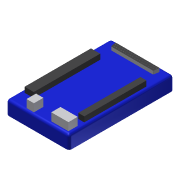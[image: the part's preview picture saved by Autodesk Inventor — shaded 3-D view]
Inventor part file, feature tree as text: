
AUTODESK INVENTOR PART (.ipt)
format: ipt  version: 2013 (Build 170138000, 138)  size: 187,904 bytes
history: native  units: in
note: dims shown in document units (in); Inventor stores cm internally (conversion verified against a paired STEP export)
features: extrude x4, sketch x4, other x3, fillet x1
ambient origin geometry x8: Origin, YZ Plane, XZ Plane, XY Plane, X Axis, Y Axis, Z Axis, Center Point
bodies: Solid1 (feature_tree), Solid2 (feature_tree), Solid3 (feature_tree), Solid4 (feature_tree)
feature tree (12):
  other  "Blocks"
  extrude  "Extrusion1"  Depth=5.0in
  extrude  "Extrusion2"  Depth=0.16in TaperAngle=0.0deg
  extrude  "Extrusion3"  Depth=0.375in TaperAngle=0.0deg
  extrude  "Extrusion4"  [1 undecoded]
  fillet  "Fillet1"  [1 undecoded]
  sketch  "Sketch2"  dims[d0=3.0in d2=5.0in]
  sketch  "Sketch3"  dims[d3=0.65in d4=0.0in d5=0.16in d6=0.0in]
  other  "DB37"
  sketch  "Sketch4"  dims[d7=0.25in d8=0.0in d9=0.375in d10=0.0in]
  sketch  "Sketch5"  dims[d11=0.125in]
  other  "DB37:1"
note: 2 required parameter values undecoded (feature->parameter linkage not recoverable at this tier; creation-order binding heuristic only, values carry confidence <= 0.55)
